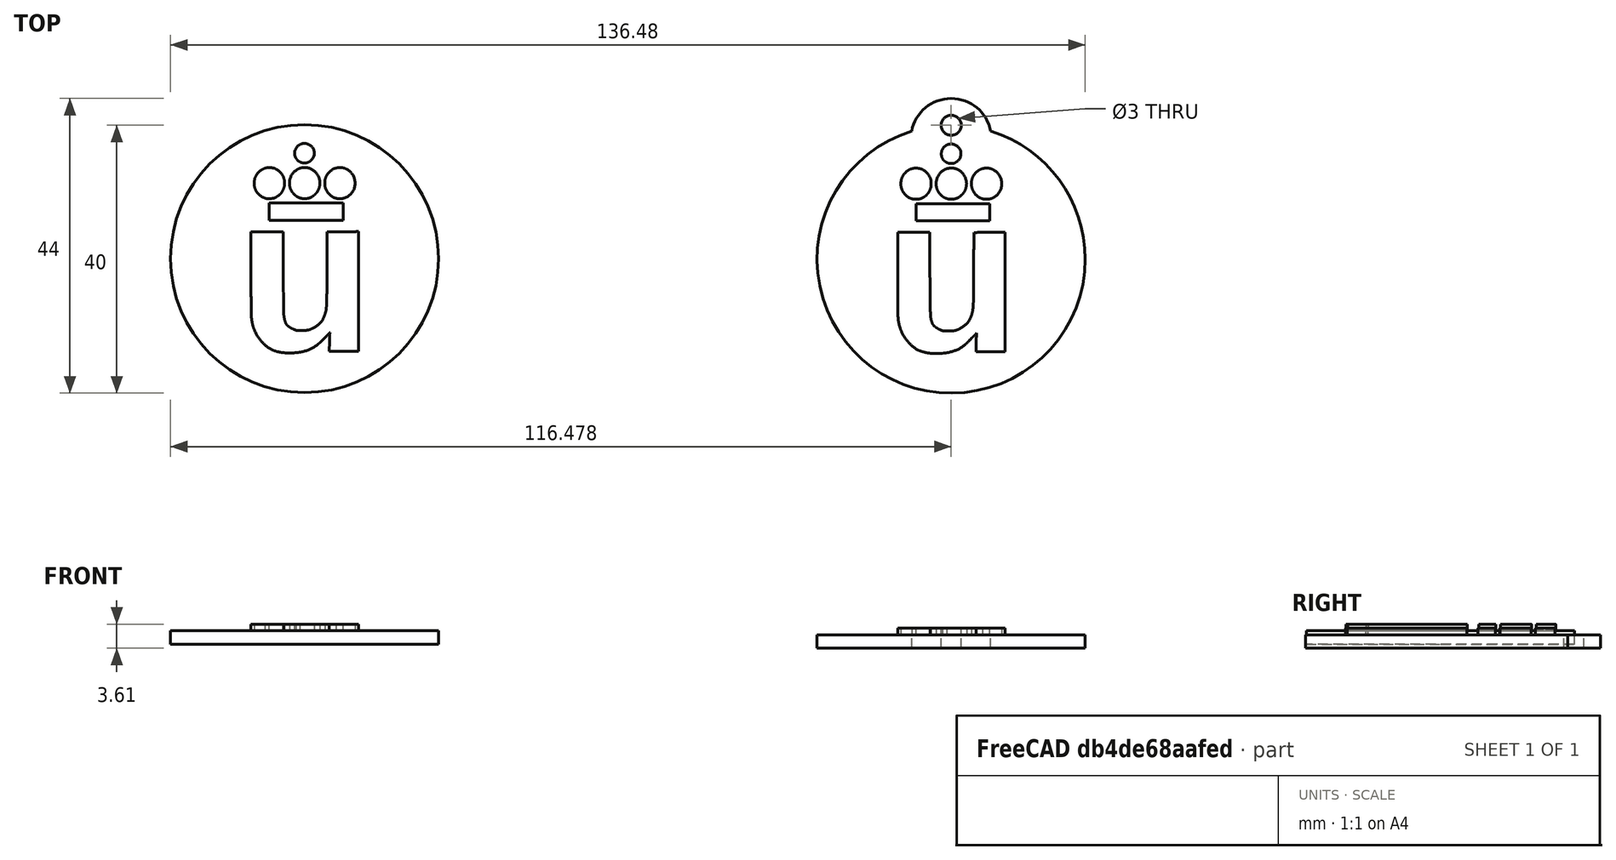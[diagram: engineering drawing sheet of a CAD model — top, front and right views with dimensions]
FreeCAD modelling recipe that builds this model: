
FCSTD DOCUMENT  (FreeCAD 0.17R12323 (Git))
Label: urjc-logo
License: All rights reserved
LicenseURL: http://en.wikipedia.org/wiki/All_rights_reserved
objects: Part::Feature×6, Part::Extrusion×6, Part::FeaturePython×5, Part::MultiFuse×4, Part::Cylinder×3, Part::Cut×1, App::DocumentObjectGroup×1
note: 25 computed .brp shape members not serialized (recipe doc carries the construction recipe); baked Part::Feature solids carry a one-line shape summary decoded from their .brp

FEATURE [Part::Feature] path4159  label="u-path"
  Placement = pos=(-19.4898,19.9388,2) rot=(0,0,1;0rad)
  shape: bbox 16.02 x 18.13 x 2e-07 mm, 0 faces, 0 solids (baked)
FEATURE [Part::Feature] path4157
  Placement = pos=(-19.4898,19.9388,2) rot=(0,0,1;0rad)
  shape: bbox 10.99 x 2.589 x 2e-07 mm, 0 faces, 0 solids (baked)
FEATURE [Part::Feature] path4155
  Placement = pos=(-19.4898,19.9388,2) rot=(0,0,1;0rad)
  shape: bbox 4.554 x 4.689 x 2e-07 mm, 0 faces, 0 solids (baked)
FEATURE [Part::Feature] path4153
  Placement = pos=(-19.4898,19.9388,2) rot=(0,0,1;0rad)
  shape: bbox 4.636 x 4.66 x 2e-07 mm, 0 faces, 0 solids (baked)
FEATURE [Part::Feature] path4151
  Placement = pos=(-19.4898,19.9388,2) rot=(0,0,1;0rad)
  shape: bbox 4.637 x 4.659 x 2e-07 mm, 0 faces, 0 solids (baked)
FEATURE [Part::Feature] path4147
  Placement = pos=(-19.4898,19.9388,2) rot=(0,0,1;0rad)
  shape: bbox 3.07 x 3.007 x 2e-07 mm, 0 faces, 0 solids (baked)
FEATURE [Part::Cylinder] Cylinder  label="coin-body1"
  Angle = 360
  AttacherType = Attacher::AttachEngine3D
  Height = 2
  Radius = 20
FEATURE [Part::Extrusion] Extrude001  label="letter-u"
  Base = -> path4159
  Dir = (0,0,-1)
  DirMode = 2
  FaceMakerClass = Part::FaceMakerBullseye
  LengthFwd = 1
  LengthRev = 0
  Reversed = true
  Solid = true
  Symmetric = false
FEATURE [Part::Extrusion] Extrude
  Base = -> path4157
  Dir = (0,0,1)
  DirMode = 0
  FaceMakerClass = Part::FaceMakerBullseye
  LengthFwd = 1
  LengthRev = 0
  Solid = true
  Symmetric = false
FEATURE [Part::Extrusion] Extrude002
  Base = -> path4155
  Dir = (0,0,1)
  DirMode = 0
  FaceMakerClass = Part::FaceMakerBullseye
  LengthFwd = 1
  LengthRev = 0
  Solid = true
  Symmetric = false
FEATURE [Part::Extrusion] Extrude003
  Base = -> path4153
  Dir = (0,0,1)
  DirMode = 0
  FaceMakerClass = Part::FaceMakerBullseye
  LengthFwd = 1
  LengthRev = 0
  Solid = true
  Symmetric = false
FEATURE [Part::Extrusion] Extrude004
  Base = -> path4151
  Dir = (0,0,1)
  DirMode = 0
  FaceMakerClass = Part::FaceMakerBullseye
  LengthFwd = 1
  LengthRev = 0
  Solid = true
  Symmetric = false
FEATURE [Part::Extrusion] Extrude005
  Base = -> path4147
  Dir = (0,0,1)
  DirMode = 0
  FaceMakerClass = Part::FaceMakerBullseye
  LengthFwd = 1
  LengthRev = 0
  Solid = true
  Symmetric = false
FEATURE [Part::Cylinder] Cylinder001  label="Cylinder"
  Angle = 360
  AttacherType = Attacher::AttachEngine3D
  Height = 10
  Placement = pos=(0,20,-3) rot=(0,0,1;0rad)
  Radius = 1.5
FEATURE [Part::MultiFuse] Fusion  label="logo-urjc"
  Shapes = -> [Extrude005,Extrude001,Extrude,Extrude002,Extrude003,Extrude004]
FEATURE [Part::FeaturePython] Clone  label="logo-urjc001"  # Draft clone (typed FeaturePython)
  AttacherType = Attacher::AttachEngine3D
  Objects = -> [Fusion]
  Scale = (1,1,1)
FEATURE [Part::FeaturePython] Clone001  label="coin-body001"  # Draft clone (typed FeaturePython)
  AttacherType = Attacher::AttachEngine3D
  Objects = -> [Cylinder]
  Scale = (1,1,1)
FEATURE [Part::Cylinder] Cylinder002  label="Cylinder001"
  Angle = 360
  AttacherType = Attacher::AttachEngine3D
  Height = 2
  Placement = pos=(0,18,0) rot=(0,0,1;0rad)
  Radius = 6
FEATURE [Part::MultiFuse] Fusion001  label="ear"
  Shapes = -> [Cylinder002,Clone001]
FEATURE [Part::Cut] Cut  label="ear-with-hole"
  Base = -> Fusion001
  Tool = -> Cylinder001
FEATURE [Part::MultiFuse] Fusion002  label="coin-logo-urjc-src"
  Shapes = -> [Cylinder,Clone]
FEATURE [Part::FeaturePython] Clone002  label="coin-logo-urjc"  # Draft clone (typed FeaturePython)
  AttacherType = Attacher::AttachEngine3D
  Objects = -> [Fusion002]
  Placement = pos=(-47.8502,0.0808975,0.605867) rot=(0,0,1;0rad)
  Scale = (1,1,1)
FEATURE [Part::FeaturePython] Clone003  label="logo-urjc002"  # Draft clone (typed FeaturePython)
  AttacherType = Attacher::AttachEngine3D
  Objects = -> [Fusion]
  Scale = (1,1,1)
FEATURE [Part::MultiFuse] Fusion003  label="coin2-logo-urjc-src"
  Shapes = -> [Cut,Clone003]
FEATURE [App::DocumentObjectGroup] Group  label="src"
  Group = -> [Fusion,Fusion002,Fusion003]
FEATURE [Part::FeaturePython] Clone004  label="coin2-logo-urjc"  # Draft clone (typed FeaturePython)
  AttacherType = Attacher::AttachEngine3D
  Objects = -> [Fusion003]
  Placement = pos=(48.6279,0,0) rot=(0,0,1;0rad)
  Scale = (1,1,1)
